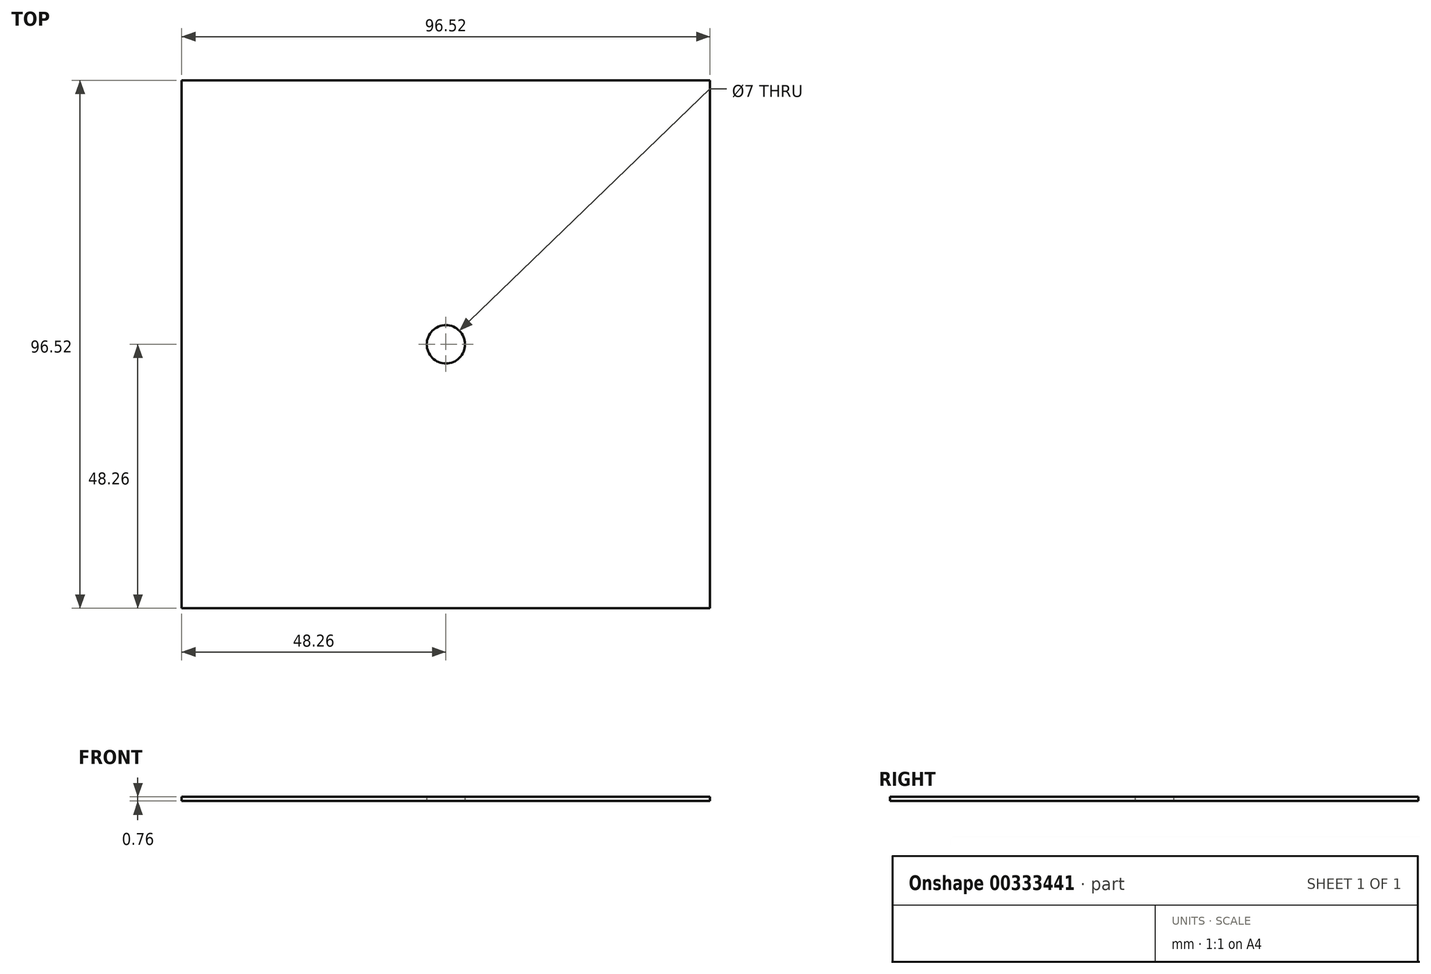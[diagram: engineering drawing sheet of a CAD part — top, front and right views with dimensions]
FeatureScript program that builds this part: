
annotation { "Feature Type Name" : "Feature", "Feature Type Description" : "" }
export const myFeature = defineFeature(function(context is Context, id is Id, definition is map)
    precondition{}
    {
        {
            var Q0;
            Q0=qCreatedBy(makeId("Top.planeOp"),FACE);
            var sketch = newSketch(context, id + "F0", { "sketchPlane" : qUnion([Q0])});
            skLineSegment(sketch, "E0.bottom", {"start": v(0, 0) * mm, "end": v(96.52, 0) * mm});
            skLineSegment(sketch, "E0.top", {"start": v(0, 96.52) * mm, "end": v(96.52, 96.52) * mm});
            skLineSegment(sketch, "E0.left", {"start": v(0, 0) * mm, "end": v(0, 96.52) * mm});
            skLineSegment(sketch, "E0.right", {"start": v(96.52, 0) * mm, "end": v(96.52, 96.52) * mm});
            skCircle(sketch, "E1", {"center": v(48.26, 48.26) * mm, "radius": 3.5 * mm});
            skSolve(sketch);
        }
        {
            var Q0;
            Q0=makeQuery(id+"F0.imprint","IMPRINT",FACE,{"disambiguationData":[TD([[makeQuery(id+"F0.imprint","IMPRINT",EDGE,{"derivedFrom":sQuery(id+"F0.wireOp",EDGE,"E0.bottom")}),1.0]])]});
            extrude(context, id + "F1", {"entities" : qUnion([Q0]), "depth" : 0.76 * mm});
        }
    });
